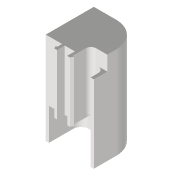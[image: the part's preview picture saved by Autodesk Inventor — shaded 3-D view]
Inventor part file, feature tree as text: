
AUTODESK INVENTOR PART (.ipt)
format: ipt  version: 2021 (Build 250183000, 183)  size: 184,832 bytes
history: native  units: mm
features: reference x16, extrude x5, sketch x5, fillet x4, other x2
ambient origin geometry x8: Origin, YZ Plane, XZ Plane, XY Plane, X Axis, Y Axis, Z Axis, Center Point
bodies: Volumenkörper1 (feature_tree)
feature tree (32):
  extrude  "Extrusion1"  Depth=20.0mm
  extrude  "Extrusion2"  TaperAngle=0.0deg  [1 undecoded]
  extrude  "Extrusion3"  Depth=10.0mm
  extrude  "Extrusion4"  Depth=5.0mm
  extrude  "Extrusion5"  Depth=2.0mm TaperAngle=0.0deg
  fillet  "Rundung1"  Radius=6.1mm
  fillet  "Rundung2"  Radius=1.2mm
  fillet  "Rundung3"  Radius=4.9mm
  fillet  "Rundung4"  Radius=5.0mm
  sketch  "Skizze1"  dims[d0=20.0mm d1=20.0mm]
  sketch  "Skizze2"  dims[d2=34.5mm d3=0.0mm d4=0.0mm d5=0.0mm]
  sketch  "Skizze3"  dims[d6=10.0mm d7=0.0mm d8=12.0mm]
  reference  "Referenz4"
  reference  "Referenz5"
  reference  "Referenz6"
  reference  "Referenz7"
  reference  "Referenz8"
  reference  "Referenz9"
  reference  "Referenz10"
  reference  "Referenz11"
  reference  "Referenz12"
  reference  "Referenz13"
  sketch  "Skizze4"  dims[d9=1.2mm d10=5.0mm]
  reference  "Referenz14"
  reference  "Referenz15"
  reference  "Referenz16"
  reference  "Referenz17"
  reference  "Referenz18"
  reference  "Referenz19"
  sketch  "Skizze5"  dims[d11=3.0mm d12=12.0mm d13=0.0mm d14=6.1mm d15=1.2mm d16=4.9mm d17=5.0mm d18=0.0mm d19=2.0mm d20=4.0mm d21=2.0mm d22=2.0mm]
  other  "Baugruppe2"
  other  "Light_Bar_Clip_-_Misumi (1):1"
note: 1 required parameter value undecoded (feature->parameter linkage not recoverable at this tier; creation-order binding heuristic only, values carry confidence <= 0.55)
